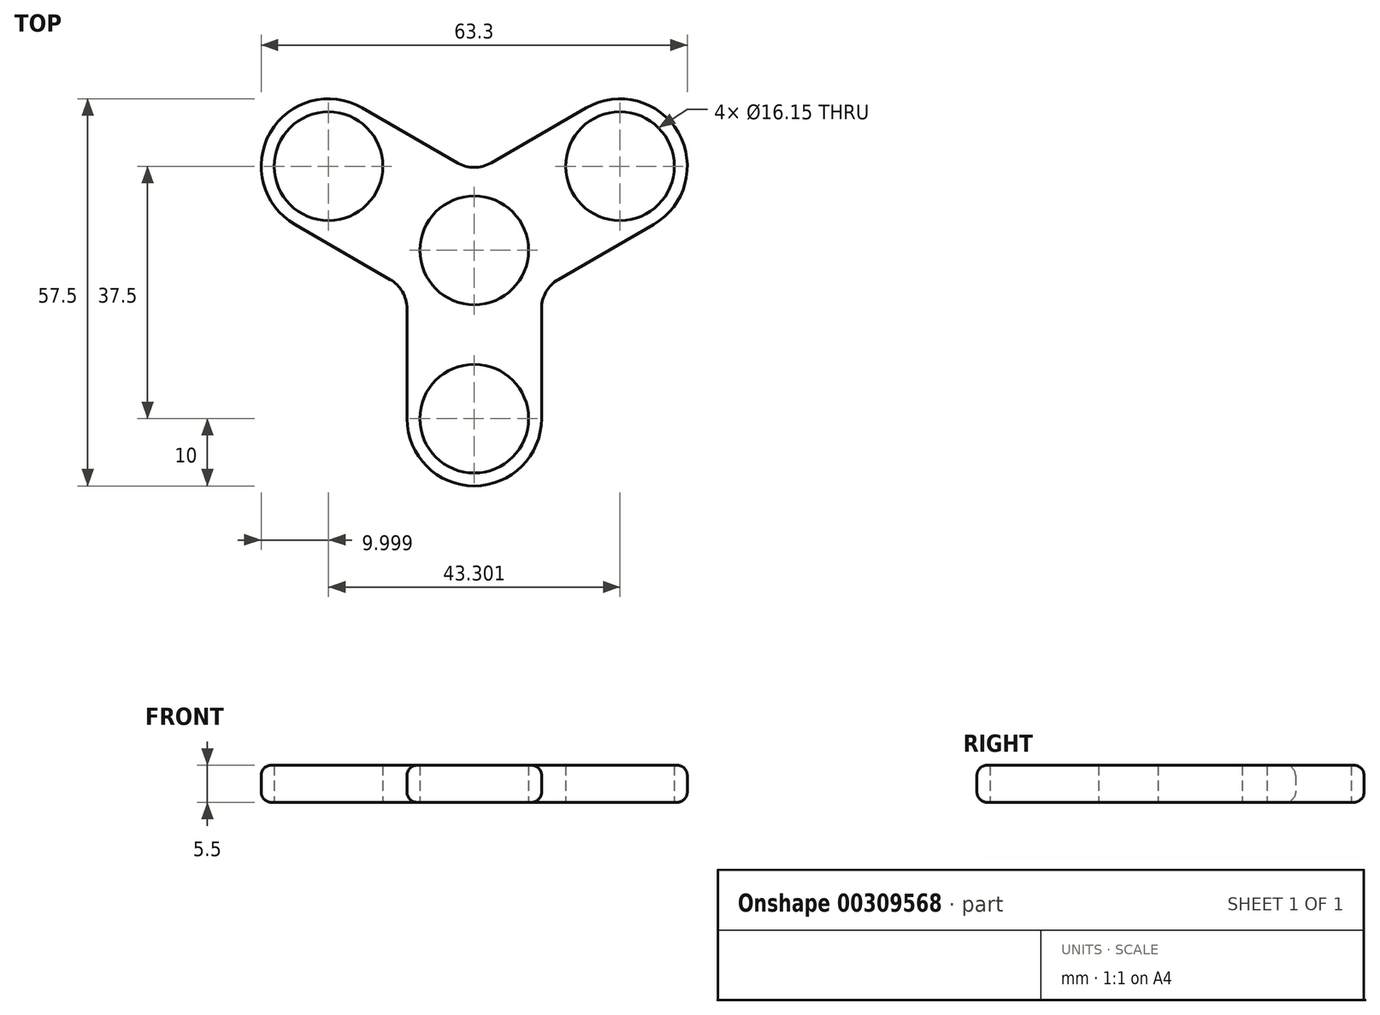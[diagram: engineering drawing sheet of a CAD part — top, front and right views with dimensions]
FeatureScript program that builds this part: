
annotation { "Feature Type Name" : "Feature", "Feature Type Description" : "" }
export const myFeature = defineFeature(function(context is Context, id is Id, definition is map)
    precondition{}
    {
        {
            var Q0;
            Q0=qCreatedBy(makeId("Top.planeOp"),FACE);
            var sketch = newSketch(context, id + "F0", { "sketchPlane" : qUnion([Q0])});
            skCircle(sketch, "E0", {"center": v(0, 0) * mm, "radius": 8 * mm});
            skCircle(sketch, "E1", {"center": v(-21.65, 12.5) * mm, "radius": 8 * mm});
            skCircle(sketch, "E2", {"center": v(21.65, 12.5) * mm, "radius": 8 * mm});
            skCircle(sketch, "E3", {"center": v(0, -25) * mm, "radius": 8 * mm});
            skLineSegment(sketch, "E4", {"start": v(0, 0) * mm, "end": v(-21.65, 12.5) * mm});
            skLineSegment(sketch, "E5", {"start": v(0, 0) * mm, "end": v(21.65, 12.5) * mm});
            skLineSegment(sketch, "E6", {"start": v(0, 0) * mm, "end": v(0, -25) * mm});
            skSolve(sketch);
        }
        {
            var Q0;
            Q0=qCreatedBy(makeId("Top.planeOp"),FACE);
            var sketch = newSketch(context, id + "F1", { "sketchPlane" : qUnion([Q0])});
            skCircle(sketch, "E7.0", {"center": v(-21.65, 12.5) * mm, "radius": 10 * mm});
            skCircle(sketch, "E8.0", {"center": v(21.65, 12.5) * mm, "radius": 10 * mm});
            skCircle(sketch, "E9.0", {"center": v(0, -25) * mm, "radius": 10 * mm});
            skLineSegment(sketch, "E10", {"start": v(0, 0) * mm, "end": v(0, 35) * mm, "construction": true});
            skLineSegment(sketch, "E11.bottom", {"start": v(31.65, 35) * mm, "end": v(-31.65, 35) * mm, "construction": true});
            skLineSegment(sketch, "E11.top", {"start": v(31.65, -35) * mm, "end": v(-31.65, -35) * mm, "construction": true});
            skLineSegment(sketch, "E11.left", {"start": v(31.65, 35) * mm, "end": v(31.65, -35) * mm, "construction": true});
            skLineSegment(sketch, "E11.right", {"start": v(-31.65, 35) * mm, "end": v(-31.65, -35) * mm, "construction": true});
            skPoint(sketch, "E11.middle", {"position": v(0, 0) * mm});
            skLineSegment(sketch, "E12.1.2", {"start": v(0, 0) * mm, "end": v(-31.65, -18.27) * mm, "construction": true});
            skLineSegment(sketch, "E12.2.2", {"start": v(0, 0) * mm, "end": v(31.65, -18.27) * mm, "construction": true});
            skLineSegment(sketch, "E13", {"start": v(-10, -5.77) * mm, "end": v(-26.65, 3.84) * mm});
            skLineSegment(sketch, "E14", {"start": v(-10, -5.77) * mm, "end": v(-10, -25) * mm});
            skLineSegment(sketch, "E15", {"start": v(0, 11.55) * mm, "end": v(-16.65, 21.16) * mm});
            skLineSegment(sketch, "E16", {"start": v(0, 11.55) * mm, "end": v(16.65, 21.16) * mm});
            skPoint(sketch, "E17", {"position": v(0, 17.5) * mm});
            skLineSegment(sketch, "E18.MirrorCS", {"start": v(-10, -5.77) * mm, "end": v(6.65, 3.84) * mm});
            skLineSegment(sketch, "E19.MirrorCS", {"start": v(10, -5.77) * mm, "end": v(26.65, 3.84) * mm});
            skLineSegment(sketch, "E20.MirrorCS", {"start": v(10, -5.77) * mm, "end": v(10, -25) * mm});
            skSolve(sketch);
        }
        {
            var Q0;
            {var subQ0=sQuery(id+"F1.wireOp",EDGE,"E7.0");var subQ1=makeQuery(id+"F1.imprint","INTERSECT",VERTEX,{"derivedFrom":[subQ0,sQuery(id+"F1.wireOp",EDGE,"E13")]});Q0=makeQuery(id+"F1.imprint","IMPRINT",FACE,{"disambiguationData":[TD([[makeQuery(id+"F1.imprint","IMPRINT",EDGE,{"disambiguationData":[TD([[subQ1,1.0]])],"derivedFrom":subQ0}),1.0]])]});}
            var Q1;
            {var subQ6=sQuery(id+"F1.wireOp",EDGE,"E13");Q1=makeQuery(id+"F1.imprint","IMPRINT",FACE,{"disambiguationData":[TD([[makeQuery(id+"F1.imprint","IMPRINT",EDGE,{"derivedFrom":subQ6}),-1.0]])]});}
            var Q2;
            {var subQ0=sQuery(id+"F1.wireOp",EDGE,"E8.0");var subQ1=makeQuery(id+"F1.imprint","INTERSECT",VERTEX,{"derivedFrom":[subQ0,sQuery(id+"F1.wireOp",EDGE,"E16")]});Q2=makeQuery(id+"F1.imprint","IMPRINT",FACE,{"disambiguationData":[TD([[makeQuery(id+"F1.imprint","IMPRINT",EDGE,{"disambiguationData":[TD([[subQ1,-1.0]])],"derivedFrom":subQ0}),1.0]])]});}
            var Q3;
            {var subQ0=sQuery(id+"F1.wireOp",EDGE,"E9.0");var subQ1=makeQuery(id+"F1.imprint","INTERSECT",VERTEX,{"derivedFrom":[subQ0,sQuery(id+"F1.wireOp",EDGE,"E14")]});Q3=makeQuery(id+"F1.imprint","IMPRINT",FACE,{"disambiguationData":[TD([[makeQuery(id+"F1.imprint","IMPRINT",EDGE,{"disambiguationData":[TD([[subQ1,1.0]])],"derivedFrom":subQ0}),1.0]])]});}
            extrude(context, id + "F2", {"entities" : qUnion([Q0, Q1, Q2, Q3]), "depth" : 5.5 * mm, "offsetDistance" : 25 * mm});
        }
        {
            var Q0;
            Q0=makeQuery(id+"F2.opExtrude","SWEPT_EDGE",EDGE,{"disambiguationData":[OSD([sQuery(id+"F1.wireOp",EDGE,"E13"),sQuery(id+"F1.wireOp",EDGE,"E14")])]});
            var Q1;
            Q1=makeQuery(id+"F2.opExtrude","SWEPT_EDGE",EDGE,{"disambiguationData":[OSD([sQuery(id+"F1.wireOp",EDGE,"E19.MirrorCS"),sQuery(id+"F1.wireOp",EDGE,"E20.MirrorCS")])]});
            var Q2;
            Q2=makeQuery(id+"F2.opExtrude","SWEPT_EDGE",EDGE,{"disambiguationData":[OSD([sQuery(id+"F1.wireOp",EDGE,"E15"),sQuery(id+"F1.wireOp",EDGE,"E16")])]});
            fillet(context, id + "F3", {"entities" : qUnion([Q0, Q1, Q2]), "radius" : 5 * mm, "tangentPropagation" : true, "allowEdgeOverflow" : false});
        }
        {
            var Q0;
            Q0=sQuery(id+"F0.wireOp",VERTEX,"E6.end");
            var Q1;
            Q1=sQuery(id+"F0.wireOp",VERTEX,"E4.end");
            var Q2;
            Q2=sQuery(id+"F0.wireOp",VERTEX,"E5.end");
            var Q3;
            Q3=sQuery(id+"F0.wireOp",VERTEX,"E4.start");
            var Q4;
            Q4=makeQuery(id+"F2.opExtrude","SWEPT_BODY",BODY,{"disambiguationData":[OSD([sQuery(id+"F1.wireOp",EDGE,"E7.0"),sQuery(id+"F1.wireOp",EDGE,"E8.0"),sQuery(id+"F1.wireOp",EDGE,"E9.0"),sQuery(id+"F1.wireOp",EDGE,"E13"),sQuery(id+"F1.wireOp",EDGE,"E14"),sQuery(id+"F1.wireOp",EDGE,"E15"),sQuery(id+"F1.wireOp",EDGE,"E16"),sQuery(id+"F1.wireOp",EDGE,"E19.MirrorCS"),sQuery(id+"F1.wireOp",EDGE,"E20.MirrorCS")])]});
            hole(context, id + "F4", {"style" : HoleStyle.SIMPLE, "endStyle" : HoleEndStyle.THROUGH, "oppositeDirection" : true, "holeDiameter" : 16.15 * mm, "majorDiameter" : 5 * mm, "isTappedThrough" : true, "tappedDepth" : 12 * mm, "tapClearance" : 3, "startFromSketch" : true, "locations" : qUnion([Q0, Q1, Q2, Q3]), "scope" : qUnion([Q4])});
        }
        {
            var Q0;
            Q0=makeQuery(id+"F2.opExtrude","CAP_EDGE",EDGE,{"disambiguationData":[OSD([sQuery(id+"F1.wireOp",EDGE,"E13")])],"isStart":false});
            var Q1;
            Q1=makeQuery(id+"F2.opExtrude","CAP_EDGE",EDGE,{"disambiguationData":[OSD([sQuery(id+"F1.wireOp",EDGE,"E14")])],"isStart":true});
            fillet(context, id + "F5", {"entities" : qUnion([Q0, Q1]), "radius" : 1.5 * mm, "tangentPropagation" : true, "allowEdgeOverflow" : false});
        }
    });
